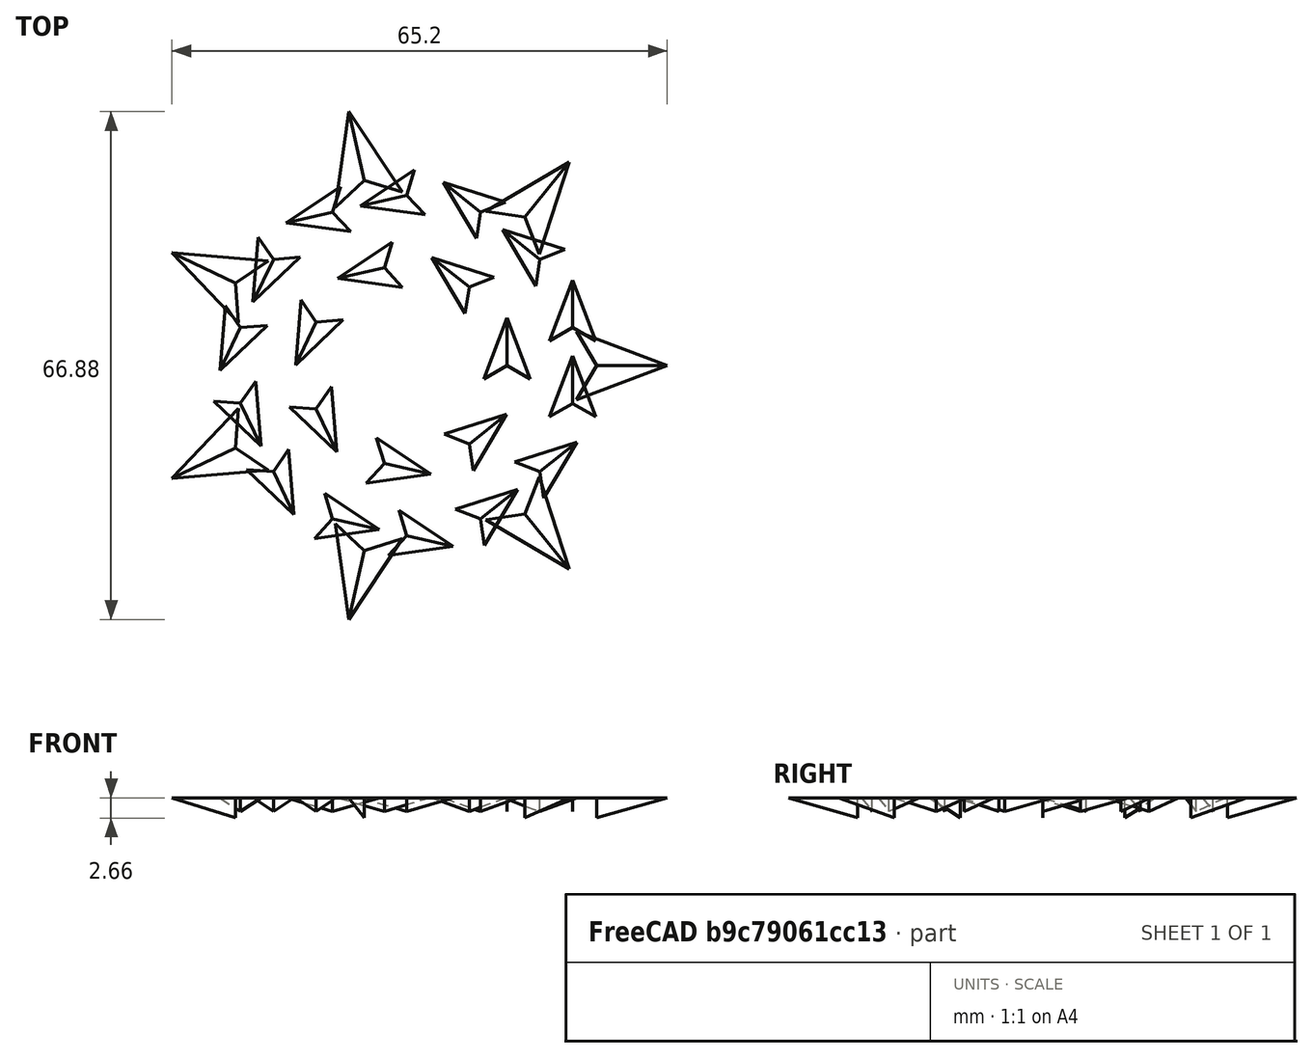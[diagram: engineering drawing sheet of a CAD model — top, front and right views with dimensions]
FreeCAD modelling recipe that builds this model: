
FCSTD DOCUMENT  (FreeCAD 0.21R32457 (Git))
Label: 10mm lens packing (cut version)
License: All rights reserved
LicenseURL: http://en.wikipedia.org/wiki/All_rights_reserved
objects: Part::FeaturePython×16, Sketcher::SketchObject×8, Part::Compound×2, App::DocumentObjectGroup×1
note: 26 computed .brp shape members not serialized (recipe doc carries the construction recipe); baked Part::Feature solids carry a one-line shape summary decoded from their .brp

FEATURE [Sketcher::SketchObject] Sketch  label="cam lens (Sketch)"
  FullyConstrained = true
  sketch-geometry (1):
    g0: Circle CenterX=0 CenterY=0 CenterZ=0 NormalX=0 NormalY=0 NormalZ=1 AngleXU=0 Radius=7.25
  constraints (2):
    c: Coincident(g0,g-1)
    c: Diameter(g0) = 14.5
FEATURE [Part::FeaturePython] PolarArray  # WARN: FeaturePython — macro-defined, semantics opaque (R4)
  Alignment = 0
  AttacherType = Attacher::AttachEngine3D
  CellStart = A1
  Count = 7
  DistributionLaw = 0
  EndInclusive = false
  ExposePlacement = false
  FlipX = false
  FlipZ = false
  GeneratorMode = 0
  MarkerShape = 1
  MarkerSize = 0
  NumElements = 7
  OrientMode = 2
  Radius = 25
  Reverse = false
  SpanEnd = 360
  SpanStart = 0
  Step = 51.4286
  Type = lattice2PolarArray2.PolarArray
  UseArcRadius = false
  UseArcRange = 0
  VSGVersion = 1
  Values = 0.0 | 51.42857142857143 | 102.85714285714286 | 154.28571428571428 | 205.71428571428572 | 257.14285714285717 | 308.57142857142856
  ValuesSource = 2
  isLattice = 1
FEATURE [Sketcher::SketchObject] Sketch001
  ExternalGeometry = -> [Sketch,PolarArray]
  FullyConstrained = false
  sketch-geometry (4):
    g0: Circle CenterX=13.2133 CenterY=0 CenterZ=0 NormalX=0 NormalY=0 NormalZ=1 AngleXU=0 Radius=5
    g1: Circle CenterX=21.8736 CenterY=5 CenterZ=0 NormalX=0 NormalY=0 NormalZ=1 AngleXU=0 Radius=5
    g2: Circle CenterX=21.8736 CenterY=-5 CenterZ=0 NormalX=0 NormalY=0 NormalZ=1 AngleXU=0 Radius=5
    g3: LineSegment StartX=39.5093 StartY=19.0267 StartZ=0 EndX=0 EndY=0 EndZ=0
  constraints (9):
    c: Equal(g1,g0)
    c: Diameter(g1) = 10
    c: Symmetric(g2,g1,g-1)
    c: PointOnObject(g0,g-1)
    c: Tangent(g0,g1)
    c: Symmetric(g-5,g-4,g3)
    c: PointOnObject(g3,g-2)
    c: Tangent(g2,g1)
    c: Equal(g2,g1)
FEATURE [Part::FeaturePython] Populate  label="Populate PolarArray with Sketch001"  # WARN: FeaturePython — macro-defined, semantics opaque (R4)
  Copying = 0
  ExposePlacement = false
  MarkerShape = 1
  MarkerSize = 0
  NumElements = 0
  Object = -> Sketch001
  OutputCompounding = 1
  PlacementsTo = -> PolarArray
  Referencing = 1
  Type = lattice2PopulateCopies.LatticePopulateCopies
  isLattice = 0
FEATURE [Part::FeaturePython] Downgrade  label="Leaves of Populate PolarArray with Sketch001"  # WARN: FeaturePython — macro-defined, semantics opaque (R4)
  Base = -> Populate
  Mode = 1
FEATURE [Sketcher::SketchObject] Sketch002  label="ext bounding (Sketch002)"
  ExternalGeometry = -> [Downgrade]
  FullyConstrained = true
  sketch-geometry (1):
    g0: Circle CenterX=-5.833e-13 CenterY=-1.0962e-12 CenterZ=0 NormalX=0 NormalY=0 NormalZ=1 AngleXU=0 Radius=27.4378
  constraints (4):
    c: Tangent(g0,g-5)
    c: Tangent(g-3,g0)
    c: Tangent(g-4,g0)
    c: Diameter(g0) = 54.8756
FEATURE [Part::FeaturePython] Placment  # WARN: FeaturePython — macro-defined, semantics opaque (R4)
  AttacherType = Attacher::AttachEngine3D
  ExposePlacement = true
  MapMode = 11
  MarkerShape = 1
  MarkerSize = 10
  NumElements = 1
  Placement = pos=(13.2133,0,0) rot=(0,0,1;1.5708rad)
  Support = -> [Downgrade]
  Type = lattice2AttachablePlacement.AttachablePlacement
  isLattice = 1
FEATURE [Part::FeaturePython] PlacementSubsequence  label="LED placements (PlacementSubsequence)"  # WARN: FeaturePython — macro-defined, semantics opaque (R4)
  Base = -> Placment
  CycleMode = 0
  ExposePlacement = false
  MarkerShape = 1
  MarkerSize = 0
  NumElements = 21
  Type = lattice2AttachablePlacement.AttachedPlacementSubsequence
  isLattice = 1
FEATURE [Sketcher::SketchObject] Sketch003  label="led footprint extents (Sketch003)"
  ExternalGeometry = -> [Downgrade]
  FullyConstrained = true
  sketch-geometry (1):
    g0: Circle CenterX=13.2133 CenterY=0 CenterZ=0 NormalX=0 NormalY=0 NormalZ=1 AngleXU=0 Radius=2.64
  constraints (2):
    c: Coincident(g0,g-3)
    c: Diameter(g0) = 5.28
FEATURE [Part::FeaturePython] Populate001  label="Populate PlacementSubsequence with Sketch003"  # WARN: FeaturePython — macro-defined, semantics opaque (R4)
  Copying = 0
  ExposePlacement = false
  MarkerShape = 1
  MarkerSize = 0
  NumElements = 0
  Object = -> Sketch003
  OutputCompounding = 1
  PlacementsTo = -> PlacementSubsequence
  Referencing = 1
  Type = lattice2PopulateCopies.LatticePopulateCopies
  isLattice = 0
FEATURE [Sketcher::SketchObject] Sketch004  label="fill zones (Sketch004)"
  ExternalGeometry = -> [Sketch002,Sketch]
  FullyConstrained = true
  sketch-geometry (11):
    g0: Circle CenterX=0 CenterY=0 CenterZ=0 NormalX=0 NormalY=0 NormalZ=1 AngleXU=0 Radius=27.0378
    g1: Circle CenterX=0 CenterY=0 CenterZ=0 NormalX=0 NormalY=0 NormalZ=1 AngleXU=0 Radius=17.1939
    g2: Circle CenterX=0 CenterY=0 CenterZ=0 NormalX=0 NormalY=0 NormalZ=1 AngleXU=0 Radius=17.4939
    g3: Circle CenterX=0 CenterY=0 CenterZ=0 NormalX=0 NormalY=0 NormalZ=1 AngleXU=0 Radius=7.65
    g4: GeomPoint X=7.65 Y=0 Z=0
    g5: GeomPoint X=17.1939 Y=0 Z=0
    g6: GeomPoint X=7.25 Y=0 Z=0
    g7: GeomPoint X=17.4939 Y=0 Z=0
    g8: GeomPoint X=27.0378 Y=0 Z=0
    g9: GeomPoint X=27.4378 Y=0 Z=0
    g10: GeomPoint X=17.3439 Y=0 Z=0
  constraints (20):
    c: Coincident(g0,g1)
    c: Coincident(g0,g2)
    c: Coincident(g0,g3)
    c: Coincident(g0,g-4)
    c: PointOnObject(g6,g-4)
    c: PointOnObject(g6,g-1)
    c: PointOnObject(g4,g3)
    c: PointOnObject(g4,g-1)
    c: PointOnObject(g5,g1)
    c: PointOnObject(g5,g-1)
    c: PointOnObject(g8,g0)
    c: PointOnObject(g8,g-1)
    c: PointOnObject(g9,g-3)
    c: PointOnObject(g9,g-1)
    c: Symmetric(g9,g6,g10)
    c: PointOnObject(g7,g2)
    c: Symmetric(g5,g7,g10)
    c: DistanceX(g6,g4) = 0.4
    c: DistanceX(g8,g9) = 0.4
    c: DistanceX(g5,g7) = 0.3
FEATURE [Part::Compound] Compound
  Links = -> [Sketch002,Sketch,Populate001,Downgrade,Sketch004]
FEATURE [Sketcher::SketchObject] Sketch005  label="connector flap (Sketch005)"
  ExternalGeometry = -> [Sketch002]
  FullyConstrained = false
  sketch-geometry (10):
    g0: LineSegment StartX=-29.2644 StartY=29.2644 StartZ=0 EndX=0 EndY=0 EndZ=0
    g1: LineSegment StartX=-24.612 StartY=26.3531 StartZ=0 EndX=-26.3531 EndY=24.612 EndZ=0
    g2: ArcOfCircle CenterX=-24.3953 CenterY=22.6541 CenterZ=0 NormalX=0 NormalY=0 NormalZ=1 AngleXU=0 Radius=2.76881 StartAngle=2.35619 EndAngle=3.92699
    g3: LineSegment StartX=-26.3531 StartY=20.6963 StartZ=0 EndX=-25.9973 EndY=20.3405 EndZ=0
    g4: ArcOfCircle CenterX=-31.0773 CenterY=15.2605 CenterZ=0 NormalX=0 NormalY=0 NormalZ=1 AngleXU=0 Radius=7.18422 StartAngle=5.82672 EndAngle=7.06858
    g5: LineSegment StartX=-20.6963 StartY=26.3531 StartZ=0 EndX=-20.3405 EndY=25.9973 EndZ=0
    g6: ArcOfCircle CenterX=-15.2605 CenterY=31.0773 CenterZ=0 NormalX=0 NormalY=0 NormalZ=1 AngleXU=0 Radius=7.18422 StartAngle=3.92699 EndAngle=5.16885
    g7: ArcOfCircle CenterX=-22.6541 CenterY=24.3953 CenterZ=0 NormalX=0 NormalY=0 NormalZ=1 AngleXU=0 Radius=2.76881 StartAngle=0.785398 EndAngle=2.35619
    g8: GeomPoint X=-19.4014 Y=19.4014 Z=0
    g9: GeomPoint X=-25.4826 Y=25.4826 Z=0
  constraints (20):
    c: Coincident(g0,g-1)
    c: Angle(g0) = -0.785398
    c: Tangent(g1,g2) = -1.5708
    c: Tangent(g2,g3) = -1.5708
    c: Tangent(g3,g4) = 1.5708
    c: Tangent(g5,g6) = -1.5708
    c: Symmetric(g6,g4,g0)
    c: Tangent(g6,g-3) = 1.5708
    c: Tangent(g4,g-3) = 1.5708
    c: Tangent(g7,g5) = 1.5708
    c: Tangent(g7,g1) = -1.5708
    c: Symmetric(g7,g2,g0)
    c: Parallel(g5,g0)
    c: Equal(g2,g7)
    c: PointOnObject(g8,g0)
    c: PointOnObject(g8,g-3)
    c: PointOnObject(g9,g0)
    c: PointOnObject(g9,g1)
    c: Distance(g9,g8) = 8.6
    c: Distance(g2,g5) = 8
FEATURE [Part::FeaturePython] Array  # Draft array (typed FeaturePython)
  Angle = 360
  ArrayType = 1
  Axis = (0,0,1)
  Base = -> Sketch005
  Center = (0,0,0)
  Count = 4
  Fuse = false
  IntervalAxis = (0,0,0)
  IntervalX = (50,0,0)
  IntervalY = (0,50,0)
  IntervalZ = (0,0,50)
  NumberCircles = 3
  NumberPolar = 4
  NumberX = 2
  NumberY = 2
  NumberZ = 1
  RadialDistance = 50
  Symmetry = 1
  TangentialDistance = 25
FEATURE [Part::FeaturePython] Array_child0  label="Array.0"  # WARN: FeaturePython — macro-defined, semantics opaque (R4)
  Base = -> Array
  FilterType = 1
  Invert = false
  OverrideMaxVal = 0
  WindowFrom = 80
  WindowTo = 100
  items = 0
FEATURE [Part::FeaturePython] Array_child1  label="Array.1"  # WARN: FeaturePython — macro-defined, semantics opaque (R4)
  Base = -> Array
  FilterType = 1
  Invert = false
  OverrideMaxVal = 0
  WindowFrom = 80
  WindowTo = 100
  items = 1
FEATURE [Part::FeaturePython] Array_child2  label="Array.2"  # WARN: FeaturePython — macro-defined, semantics opaque (R4)
  Base = -> Array
  FilterType = 1
  Invert = false
  OverrideMaxVal = 0
  WindowFrom = 80
  WindowTo = 100
  items = 2
FEATURE [Part::FeaturePython] Array_child3  label="Array.3"  # WARN: FeaturePython — macro-defined, semantics opaque (R4)
  Base = -> Array
  FilterType = 1
  Invert = false
  OverrideMaxVal = 0
  WindowFrom = 80
  WindowTo = 100
  items = 3
FEATURE [App::DocumentObjectGroup] GrExplode_Array  label="Exploded Array"
  Group = -> [Array_child0,Array_child1,Array_child2,Array_child3]
FEATURE [Part::FeaturePython] Connect  # WARN: FeaturePython — macro-defined, semantics opaque (R4)
  Objects = -> [Array_child0,Sketch002]
  Tolerance = 0
FEATURE [Part::FeaturePython] Connect001  # WARN: FeaturePython — macro-defined, semantics opaque (R4)
  Objects = -> [Connect,Array_child1]
  Tolerance = 0
FEATURE [Part::FeaturePython] Connect002  # WARN: FeaturePython — macro-defined, semantics opaque (R4)
  Objects = -> [Connect001,Array_child3]
  Tolerance = 0
FEATURE [Part::FeaturePython] Connect003  # WARN: FeaturePython — macro-defined, semantics opaque (R4)
  Objects = -> [Connect002,Array_child2]
  Tolerance = 0
FEATURE [Part::Compound] Compound001  label="board outline"
  Links = -> [Sketch,Connect003]
FEATURE [Sketcher::SketchObject] Sketch006
  FullyConstrained = false
  sketch-geometry (2):
    g0: LineSegment StartX=-35.5698 StartY=35.5698 StartZ=0 EndX=0 EndY=0 EndZ=0
    g1: Circle CenterX=-22 CenterY=22 CenterZ=0 NormalX=0 NormalY=0 NormalZ=1 AngleXU=0 Radius=1.6
  constraints (5):
    c: Angle(g0) = -0.785398
    c: Coincident(g0,g-1)
    c: Diameter(g1) = 3.2
    c: PointOnObject(g1,g0)
    c: DistanceX(g-2,g1) = -22
FEATURE [Sketcher::SketchObject] Sketch007
  ExternalGeometry = -> [Connect003,Sketch,Populate]
  FullyConstrained = false
  sketch-geometry (5):
    g0: LineSegment StartX=-20.6963 StartY=26.3531 StartZ=0 EndX=-5.88998 EndY=11.5468 EndZ=0
    g1: ArcOfCircle CenterX=-9.51851 CenterY=7.91832 CenterZ=0 NormalX=0 NormalY=0 NormalZ=1 AngleXU=0 Radius=5.13151 StartAngle=5.5893 EndAngle=7.06858
    g2: ArcOfCircle CenterX=22.6218 CenterY=-3.80068 CenterZ=0 NormalX=0 NormalY=0 NormalZ=1 AngleXU=0 Radius=4.49894 StartAngle=6.11673 EndAngle=7.32524
    g3: LineSegment StartX=24.8913 StartY=0.0838922 StartZ=0 EndX=16.2215 EndY=5.149 EndZ=0
    g4: ArcOfCircle CenterX=13.2133 CenterY=0 CenterZ=0 NormalX=0 NormalY=0 NormalZ=1 AngleXU=0 Radius=5.96334 StartAngle=1.04205 EndAngle=3.14159
  constraints (8):
    c: Tangent(g0,g1) = 1.5708
    c: Tangent(g1,g-4) = 1.5708
    c: Tangent(g0,g-3) = 1.5708
    c: Tangent(g2,g3) = -1.5708
    c: Tangent(g3,g4) = -1.5708
    c: Coincident(g4,g-7)
    c: Tangent(g4,g-4) = 1.5708
    c: Tangent(g2,g-5) = -1.5708
FEATURE [Part::FeaturePython] Connect004  # WARN: FeaturePython — macro-defined, semantics opaque (R4)
  Objects = -> [Connect003,Sketch007,Sketch]
  Tolerance = 0
